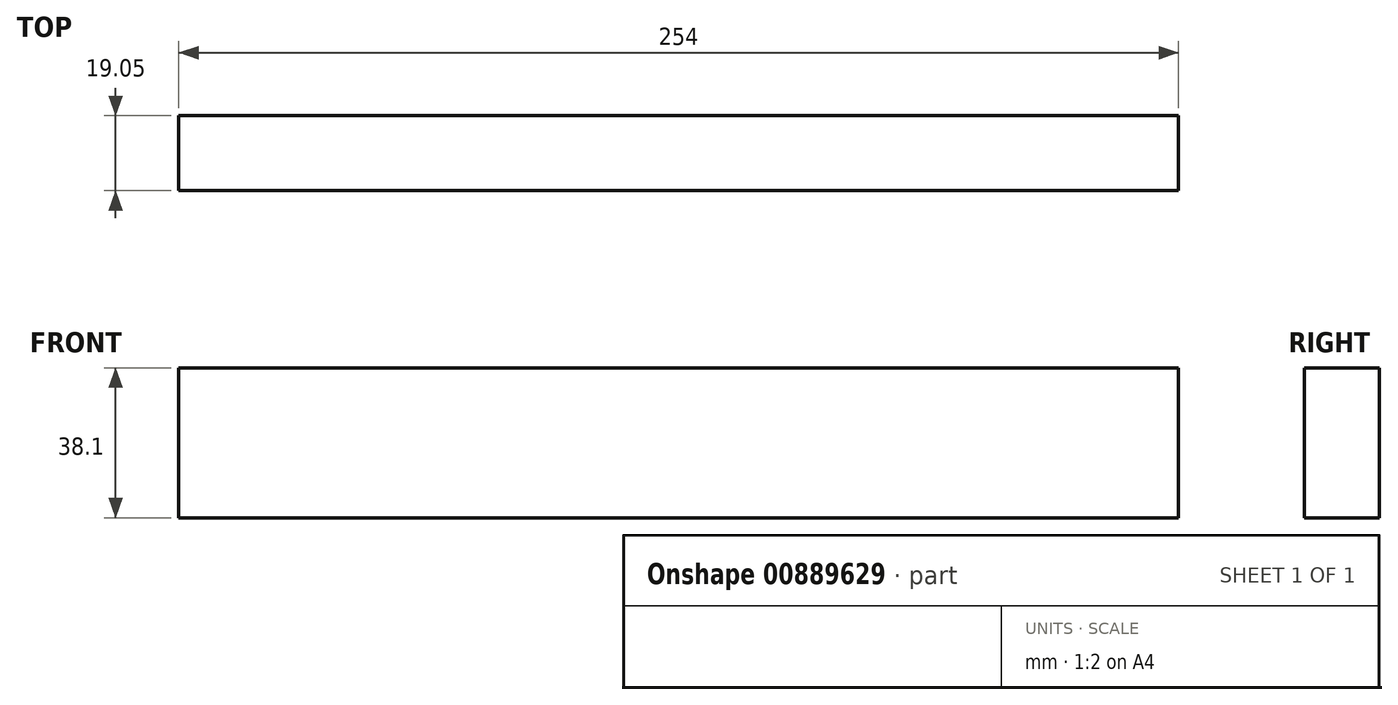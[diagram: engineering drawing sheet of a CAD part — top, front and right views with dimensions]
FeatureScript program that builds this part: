
annotation { "Feature Type Name" : "Feature", "Feature Type Description" : "" }
export const myFeature = defineFeature(function(context is Context, id is Id, definition is map)
    precondition{}
    {
        {
            var Q0;
            Q0=qCreatedBy(makeId("Right.planeOp"),FACE);
            var sketch = newSketch(context, id + "F0", { "sketchPlane" : qUnion([Q0])});
            skLineSegment(sketch, "E0.bottom", {"start": v(0, 0) * mm, "end": v(19.05, 0) * mm});
            skLineSegment(sketch, "E0.top", {"start": v(0, 38.1) * mm, "end": v(19.05, 38.1) * mm});
            skLineSegment(sketch, "E0.left", {"start": v(0, 0) * mm, "end": v(0, 38.1) * mm});
            skLineSegment(sketch, "E0.right", {"start": v(19.05, 0) * mm, "end": v(19.05, 38.1) * mm});
            skSolve(sketch);
        }
        {
            var Q0;
            Q0 = qSketchRegion(id + "F0", true);
            extrude(context, id + "F1", {"entities" : qUnion([Q0]), "depth" : 254 * mm, "offsetDistance" : 25.4 * mm});
        }
    });
